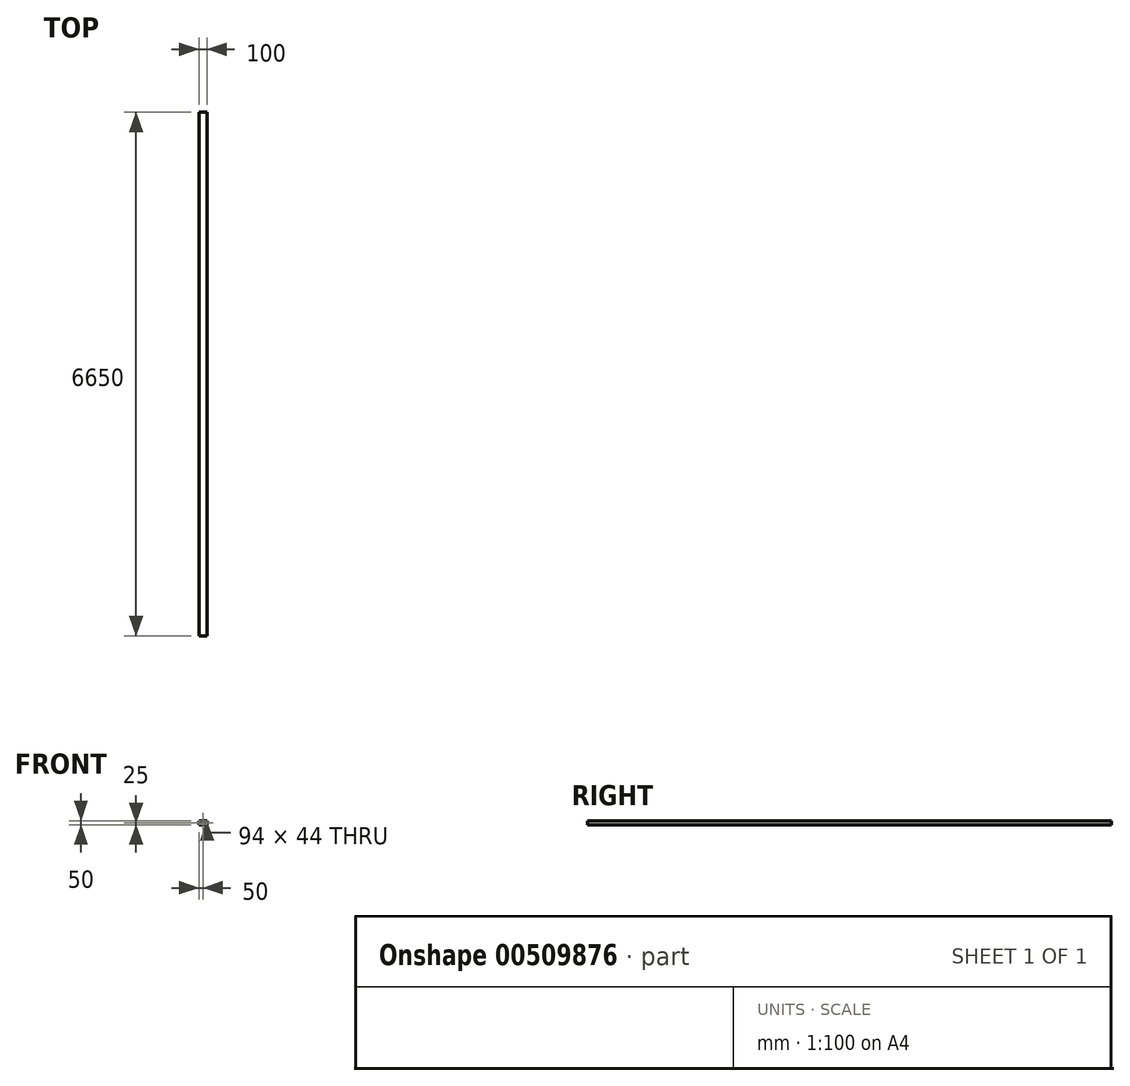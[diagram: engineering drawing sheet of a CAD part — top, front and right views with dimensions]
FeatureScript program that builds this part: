
annotation { "Feature Type Name" : "Feature", "Feature Type Description" : "" }
export const myFeature = defineFeature(function(context is Context, id is Id, definition is map)
    precondition{}
    {
        {
            var Q0;
            Q0=qCreatedBy(makeId("Front.planeOp"),FACE);
            var sketch = newSketch(context, id + "F0", { "sketchPlane" : qUnion([Q0])});
            skLineSegment(sketch, "E0.bottom", {"start": v(50, -25) * mm, "end": v(-50, -25) * mm});
            skLineSegment(sketch, "E0.top", {"start": v(50, 25) * mm, "end": v(-50, 25) * mm});
            skLineSegment(sketch, "E0.left", {"start": v(50, -25) * mm, "end": v(50, 25) * mm});
            skLineSegment(sketch, "E0.right", {"start": v(-50, -25) * mm, "end": v(-50, 25) * mm});
            skPoint(sketch, "E0.middle", {"position": v(0, 0) * mm});
            skLineSegment(sketch, "E1.bottom", {"start": v(47, -22) * mm, "end": v(-47, -22) * mm});
            skLineSegment(sketch, "E1.top", {"start": v(47, 22) * mm, "end": v(-47, 22) * mm});
            skLineSegment(sketch, "E1.left", {"start": v(47, -22) * mm, "end": v(47, 22) * mm});
            skLineSegment(sketch, "E1.right", {"start": v(-47, -22) * mm, "end": v(-47, 22) * mm});
            skSolve(sketch);
        }
        {
            var Q0;
            Q0=makeQuery(id+"F0.imprint","IMPRINT",FACE,{"disambiguationData":[TD([[makeQuery(id+"F0.imprint","IMPRINT",EDGE,{"derivedFrom":sQuery(id+"F0.wireOp",EDGE,"E0.bottom")}),-1.0]])]});
            extrude(context, id + "F1", {"entities" : qUnion([Q0]), "depth" : 6650 * mm, "offsetDistance" : 25 * mm});
        }
    });
